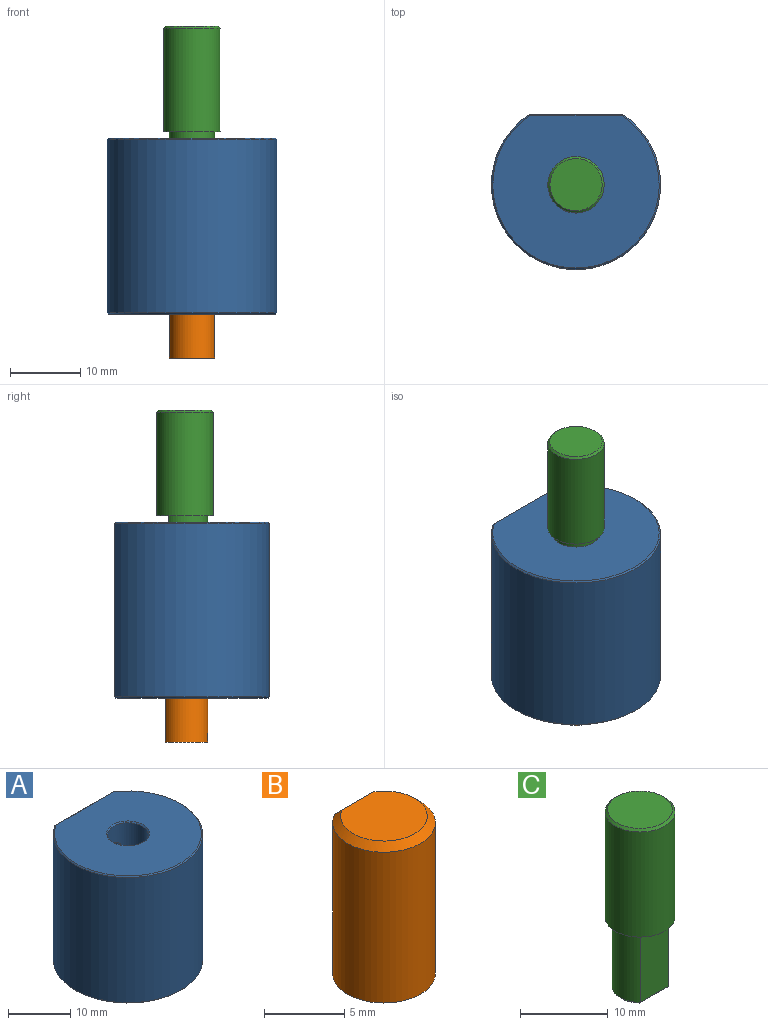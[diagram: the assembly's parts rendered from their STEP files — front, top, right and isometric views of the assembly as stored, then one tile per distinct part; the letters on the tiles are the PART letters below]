
ASSEMBLY  parts=3 mates=4
PART A: 13 faces, bbox 24x22x25 mm
  f0: plane 24.6x13.27mm, normal (0,1,0), area 312.2mm2, adj f2,f5,f6,f9,f12
  f1: cylinder r=3.25mm len=24.6mm, axis (0,0,-1), area 487.8mm2, adj f5,f6,f7,f10
  f2: cylinder r=12mm len=24.6mm, axis (0,0,-1), area 1509mm2, adj f0,f8,f11
  f3: plane 23.6x21.6mm, normal (0,0,1), area 382.2mm2, adj f10,f11,f12
  f4: plane 23.6x21.6mm, normal (0,0,-1), area 382.2mm2, adj f7,f8,f9
  f5: cylinder r=1.5mm len=7.12mm, axis (0,1,0), area 65.3mm2, adj f0,f1
  f6: cylinder r=1.5mm len=7.12mm, axis (0,1,0), area 65.3mm2, adj f0,f1
  f7: cone r=3.45mm half-angle=45deg, axis (0,0,-1), area 6mm2, adj f1,f4
  f8: cone r=12mm half-angle=45deg, axis (0,0,1), area 17.2mm2, adj f2,f4,f9
  f9: plane 13.27x0.2mm, normal (0,0.71,-0.71), area 3.7mm2, adj f0,f4,f8
  f10: cone r=3.25mm half-angle=45deg, axis (0,0,1), area 6mm2, adj f1,f3
  f11: cone r=11.8mm half-angle=45deg, axis (0,0,-1), area 17.2mm2, adj f2,f3,f12
  f12: plane 13.27x0.2mm, normal (0,0.71,0.71), area 3.7mm2, adj f0,f3,f11
PART B: 6 faces, bbox 6.4x6x12 mm
  f0: plane 11.5x3.1mm, normal (0,1,0), area 35.6mm2, adj f1,f3,f5
  f1: cylinder r=3.2mm len=11.5mm, axis (0,0,-1), area 194mm2, adj f0,f3,f4
  f2: plane 5.4x5mm, normal (0,0,1), area 22.1mm2, adj f4,f5
  f3: plane 6.4x6mm, normal (0,0,-1), area 31.3mm2, adj f0,f1
  f4: cone r=2.7mm half-angle=45deg, axis (0,0,-1), area 10.9mm2, adj f1,f2,f5
  f5: plane 3.11x0.51mm, normal (0,0.71,0.71), area 2.1mm2, adj f0,f2,f4
PART C: 9 faces, bbox 8x8x25 mm
  f0: plane 8x8mm, normal (0,0,-1), area 20.9mm2, adj f1,f3,f4
  f1: cylinder r=4mm len=14.7mm, axis (0,0,-1), area 369.5mm2, adj f0,f6
  f2: plane 7.4x7.4mm, normal (0,0,1), area 43mm2, adj f6
  f3: plane 9.7x4.45mm, normal (0,-1,0), area 43.2mm2, adj f0,f4,f8
  f4: cylinder r=3.2mm len=9.7mm, axis (0,0,1), area 147.3mm2, adj f0,f3,f7
  f5: plane 5.8x4.9mm, normal (0,0,-1), area 23.8mm2, adj f7,f8
  f6: cone r=3.7mm half-angle=45deg, axis (0,0,-1), area 10.3mm2, adj f1,f2
  f7: cone r=2.9mm half-angle=45deg, axis (0,0,1), area 6.1mm2, adj f4,f5,f8
  f8: plane 4.45x0.3mm, normal (0,-0.71,-0.71), area 1.8mm2, adj f3,f5,f7
PLACE A t=(10.35,10.47,-1.05)mm
PLACE B t=(10.35,10.47,-7.25)mm fixed
PLACE C rot(axis=(0,0,1),180deg) t=(10.35,10.47,24.85)mm
MATE parallel A.f0 <-> B.f0  axis (0,1,0) through (10.35,20.47,11.45)mm
MATE cylindrical C.f4 <-> B.f1  axis (0,0,-1) through (10.35,10.47,15.15)mm
MATE parallel C.f3 <-> A.f0  axis (0,1,0) through (10.35,12.77,20)mm
MATE cylindrical B.f1 <-> A.f1  axis (0,0,-1) through (10.35,10.47,-7.25)mm
